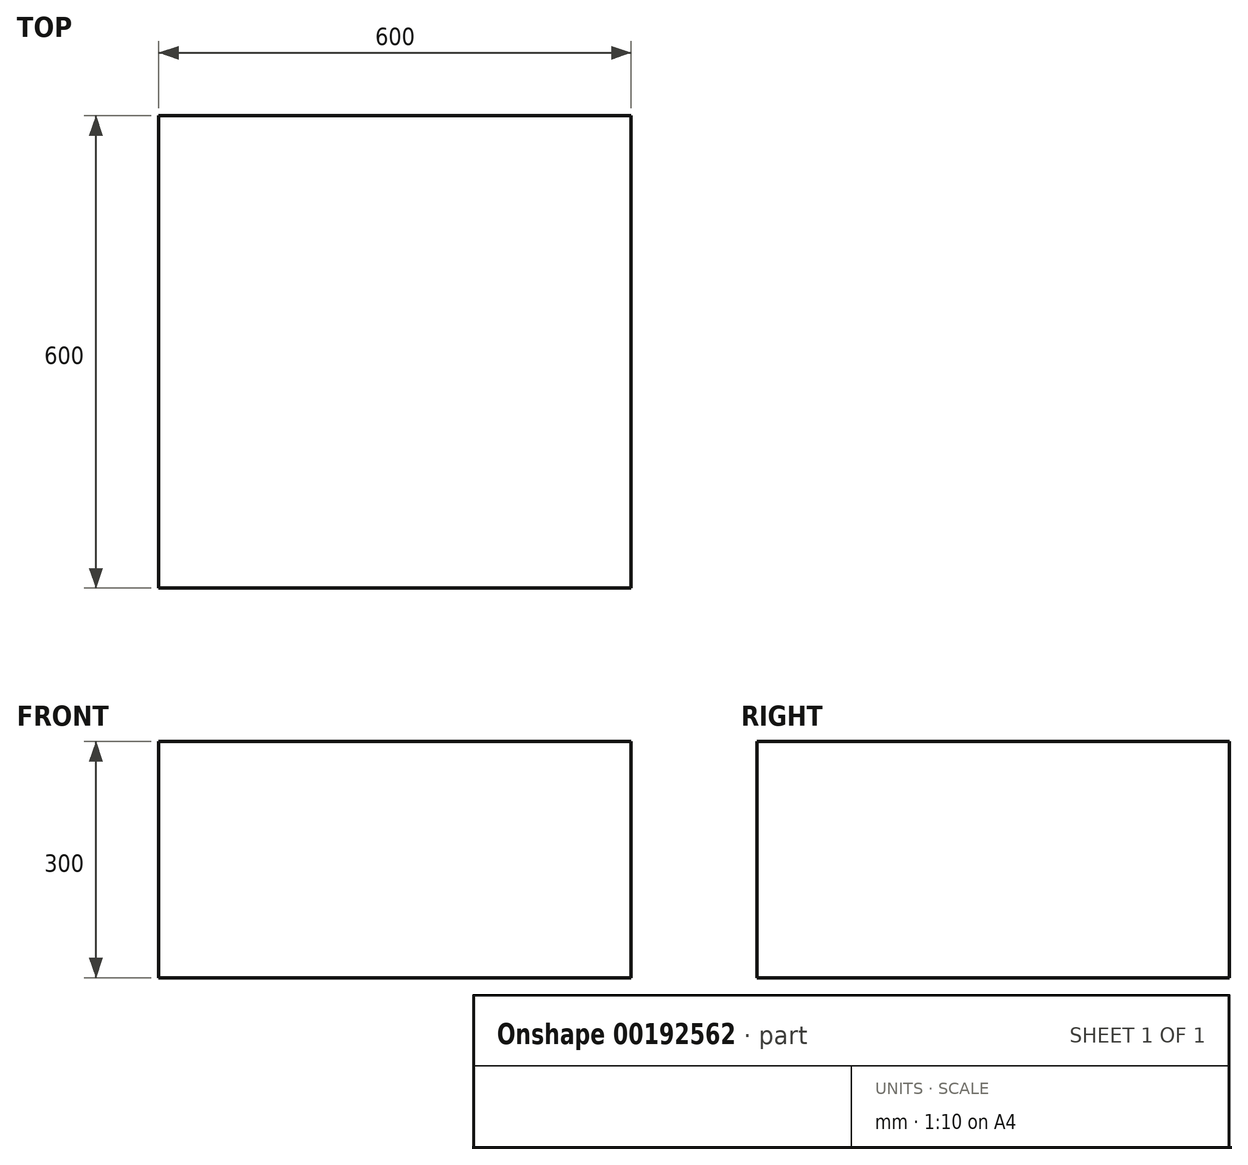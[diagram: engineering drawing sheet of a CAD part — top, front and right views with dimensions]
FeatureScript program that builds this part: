
annotation { "Feature Type Name" : "Feature", "Feature Type Description" : "" }
export const myFeature = defineFeature(function(context is Context, id is Id, definition is map)
    precondition{}
    {
        {
            var Q0;
            Q0=qCreatedBy(makeId("Top.planeOp"),FACE);
            var sketch = newSketch(context, id + "F0", { "sketchPlane" : qUnion([Q0])});
            skLineSegment(sketch, "E0.bottom", {"start": v(300, -300) * mm, "end": v(-300, -300) * mm});
            skLineSegment(sketch, "E0.top", {"start": v(300, 300) * mm, "end": v(-300, 300) * mm});
            skLineSegment(sketch, "E0.left", {"start": v(300, -300) * mm, "end": v(300, 300) * mm});
            skLineSegment(sketch, "E0.right", {"start": v(-300, -300) * mm, "end": v(-300, 300) * mm});
            skPoint(sketch, "E0.middle", {"position": v(0, 0) * mm});
            skSolve(sketch);
        }
        {
            var Q0;
            Q0 = qSketchRegion(id + "F0", true);
            extrude(context, id + "F1", {"entities" : qUnion([Q0]), "depth" : 300 * mm});
        }
    });
